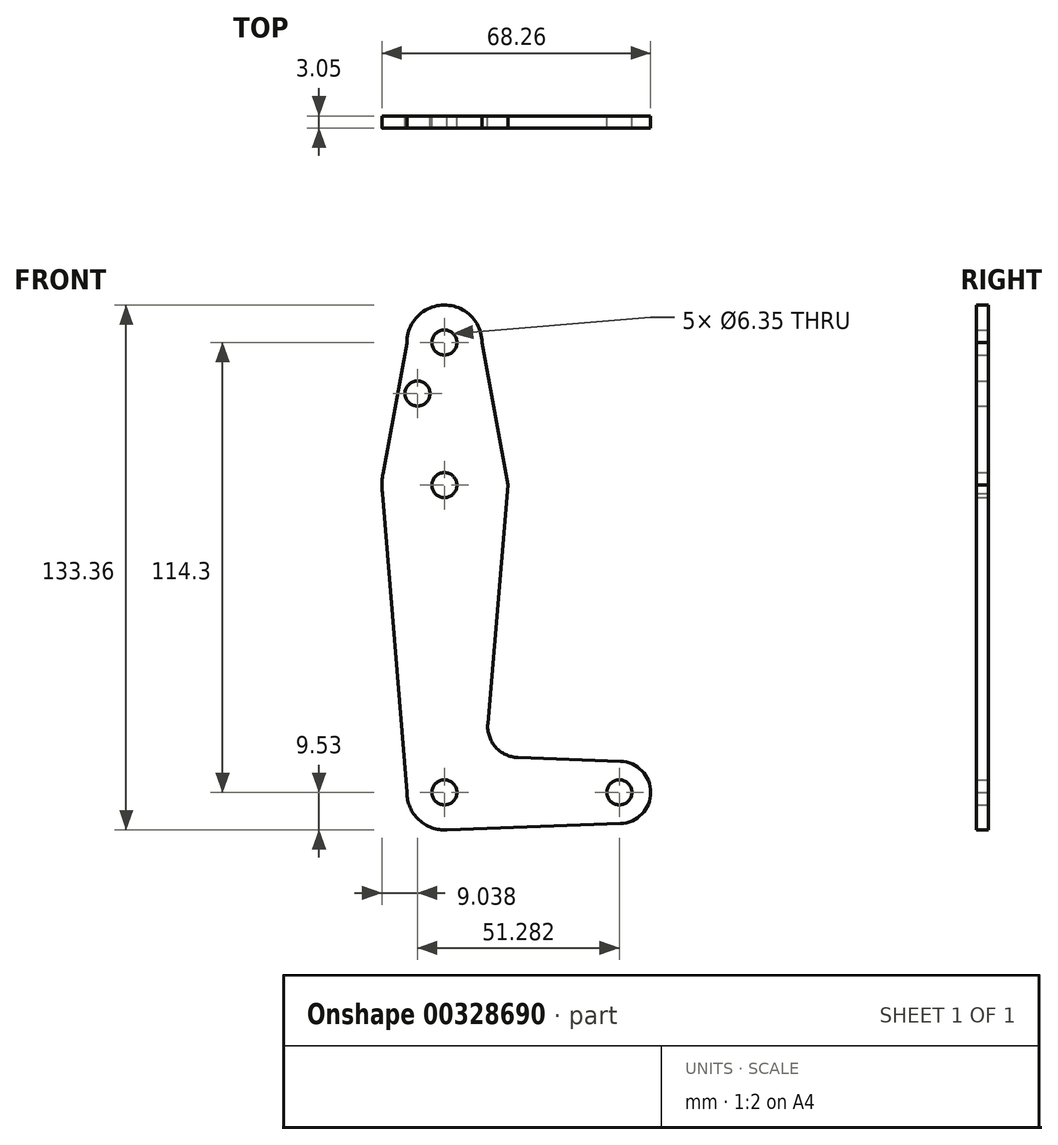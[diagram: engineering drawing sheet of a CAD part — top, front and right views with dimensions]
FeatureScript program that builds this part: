
annotation { "Feature Type Name" : "Feature", "Feature Type Description" : "" }
export const myFeature = defineFeature(function(context is Context, id is Id, definition is map)
    precondition{}
    {
        {
            var Q0;
            Q0=qCreatedBy(makeId("Front.planeOp"),FACE);
            var sketch = newSketch(context, id + "F0", { "sketchPlane" : qUnion([Q0])});
            skLineSegment(sketch, "E0", {"start": v(0, 0) * mm, "end": v(0, 114.3) * mm, "construction": true});
            skLineSegment(sketch, "E1", {"start": v(0, 0) * mm, "end": v(44.45, 0) * mm, "construction": true});
            skCircle(sketch, "E2", {"center": v(44.45, 0) * mm, "radius": 7.94 * mm});
            skCircle(sketch, "E3", {"center": v(0, 78.07) * mm, "radius": 15.88 * mm});
            skCircle(sketch, "E4", {"center": v(0, 114.3) * mm, "radius": 9.53 * mm});
            skLineSegment(sketch, "E5", {"start": v(-15.87, 77.68) * mm, "end": v(-15.62, 75.26) * mm});
            skPoint(sketch, "E6.trimOffspring.end.orphan", {"position": v(-7.98, 0) * mm});
            skCircle(sketch, "E7", {"center": v(0, 0) * mm, "radius": 9.53 * mm});
            skLineSegment(sketch, "E8", {"start": v(0, -9.52) * mm, "end": v(44.73, -7.93) * mm});
            skLineSegment(sketch, "E9", {"start": v(-15.87, 77.68) * mm, "end": v(-9.52, 0) * mm});
            skLineSegment(sketch, "E10", {"start": v(9.52, 114.3) * mm, "end": v(16.13, 78.14) * mm});
            skLineSegment(sketch, "E11", {"start": v(16.13, 78.14) * mm, "end": v(11.03, 17.47) * mm});
            skLineSegment(sketch, "E12", {"start": v(18.67, 8.86) * mm, "end": v(44.73, 7.93) * mm});
            skCircle(sketch, "E13", {"center": v(0, 114.3) * mm, "radius": 3.18 * mm});
            skLineSegment(sketch, "E14", {"start": v(-9.52, 114.16) * mm, "end": v(-15.61, 80.93) * mm});
            skCircle(sketch, "E15", {"center": v(-6.83, 101.35) * mm, "radius": 3.18 * mm});
            skCircle(sketch, "E16", {"center": v(0, 0) * mm, "radius": 3.18 * mm});
            skCircle(sketch, "E17", {"center": v(44.45, 0) * mm, "radius": 3.18 * mm});
            skCircle(sketch, "E18", {"center": v(0, 78.07) * mm, "radius": 3.18 * mm});
            skArc(sketch, "E19.filletArc", {"start": v(11.03, 17.47) * mm, "mid": v(13, 11.53) * mm, "end": v(18.67, 8.86) * mm});
            skSolve(sketch);
        }
        {
            var Q0;
            Q0 = qSketchRegion(id + "F0", true);
            extrude(context, id + "F1", {"entities" : qUnion([Q0]), "depth" : 3.05 * mm});
        }
    });
